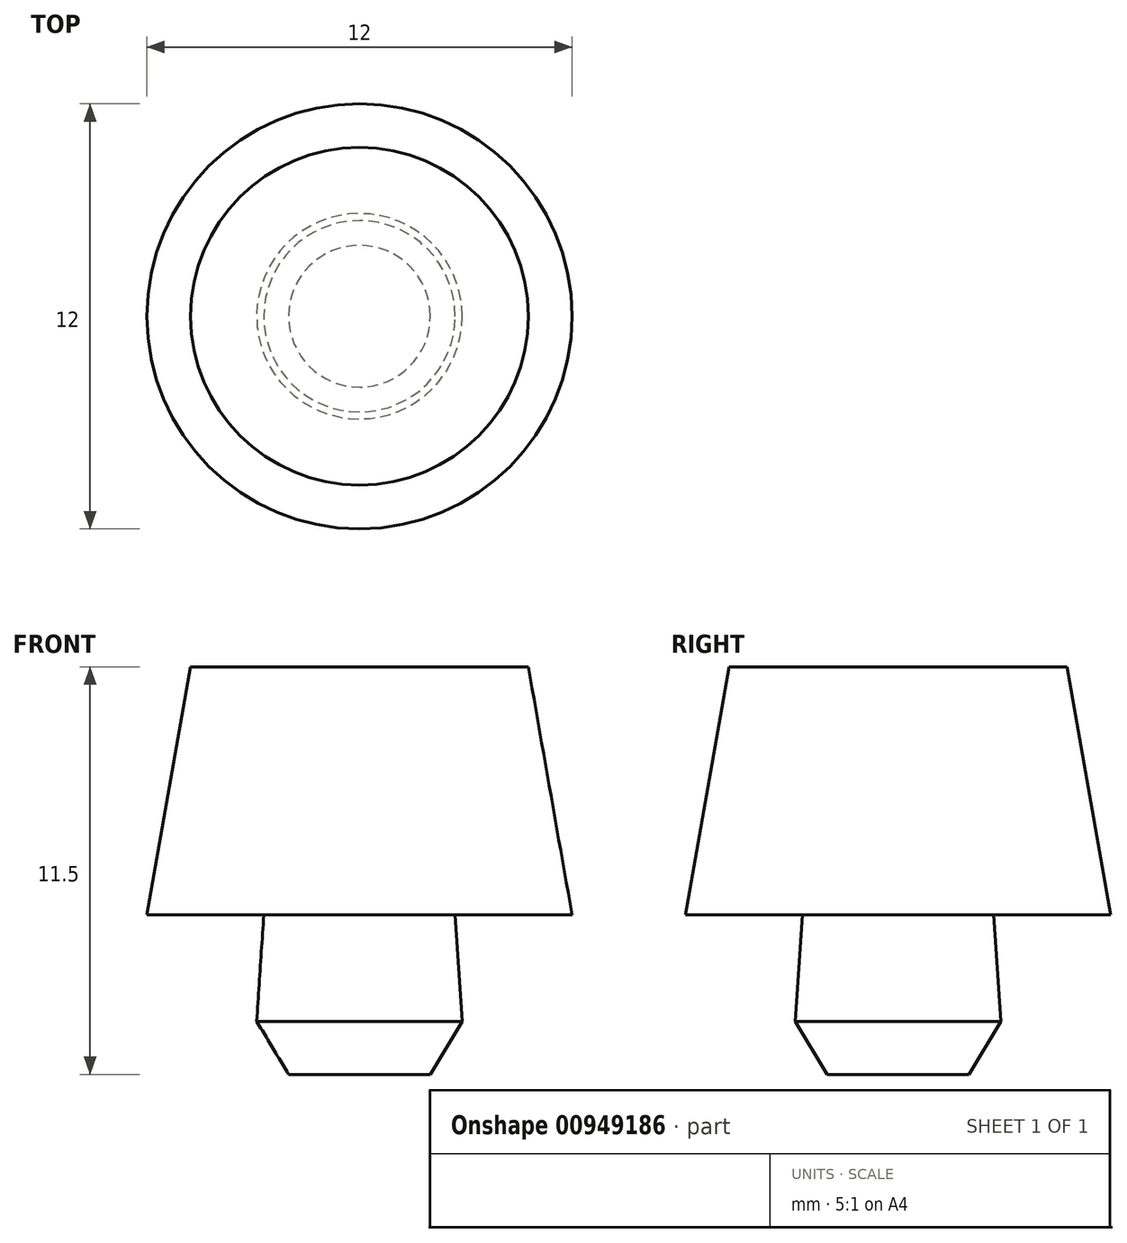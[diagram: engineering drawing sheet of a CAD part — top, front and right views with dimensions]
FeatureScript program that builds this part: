
annotation { "Feature Type Name" : "Feature", "Feature Type Description" : "" }
export const myFeature = defineFeature(function(context is Context, id is Id, definition is map)
    precondition{}
    {
        {
            var Q0;
            Q0=qCreatedBy(makeId("Top.planeOp"),FACE);
            var sketch = newSketch(context, id + "F0", { "sketchPlane" : qUnion([Q0])});
            skCircle(sketch, "E0", {"center": v(0, 0) * mm, "radius": 6 * mm});
            skSolve(sketch);
        }
        {
            var Q0;
            Q0=makeQuery(id+"F0.imprint","IMPRINT",FACE,{"disambiguationData":[TD([[makeQuery(id+"F0.imprint","IMPRINT",EDGE,{"derivedFrom":sQuery(id+"F0.wireOp",EDGE,"E0")}),1.0]])]});
            var Q1;
            Q1=makeQuery(id+"F0.imprint","IMPRINT",FACE,{"disambiguationData":[TD([[makeQuery(id+"F0.imprint","IMPRINT",EDGE,{"derivedFrom":sQuery(id+"F0.wireOp",EDGE,"QOBQSCr0-Hx2Y-VHzB-GS9c-7p1tTEKiA8WD")}),1.0]])]});
            extrude(context, id + "F1", {"entities" : qUnion([Q0, Q1]), "depth" : 7 * mm, "offsetDistance" : 25 * mm, "hasDraft" : true, "draftAngle" : 10 * degree, "draftPullDirection" : true});
        }
        {
            var Q0;
            Q0=qCreatedBy(makeId("Front.planeOp"),FACE);
            var sketch = newSketch(context, id + "F2", { "sketchPlane" : qUnion([Q0])});
            skLineSegment(sketch, "E1", {"start": v(0, 0) * mm, "end": v(-2.7, 0) * mm});
            skLineSegment(sketch, "E2", {"start": v(-2.7, 0) * mm, "end": v(-2.9, -3) * mm});
            skLineSegment(sketch, "E3", {"start": v(-2.9, -3) * mm, "end": v(-2, -4.5) * mm});
            skLineSegment(sketch, "E4", {"start": v(-2, -4.5) * mm, "end": v(0, -4.5) * mm});
            skLineSegment(sketch, "E5", {"start": v(0, -4.5) * mm, "end": v(0, 0) * mm});
            skLineSegment(sketch, "E6", {"start": v(-2.9, -3) * mm, "end": v(0, -3) * mm, "construction": true});
            skSolve(sketch);
        }
        {
            var Q0;
            Q0=makeQuery(id+"F2.imprint","IMPRINT",FACE,{"disambiguationData":[TD([[makeQuery(id+"F2.imprint","IMPRINT",EDGE,{"derivedFrom":sQuery(id+"F2.wireOp",EDGE,"E1")}),1.0]])]});
            var Q1;
            Q1=sQuery(id+"F2.wireOp",EDGE,"E5");
            revolve(context, id + "F3", {"operationType" : NewBodyOperationType.ADD, "surfaceOperationType" : NewSurfaceOperationType.NEW, "entities" : qUnion([Q0]), "axis" : qUnion([Q1]), "revolveType" : RevolveType.FULL});
        }
    });
